# Revit family: EUBPRO-SM_Ceiling Hosted_R16_V1.0
name_source: partatom
category: Lighting Fixtures
revit_build: Autodesk Revit 2016 (Build: 20150220_1215(x64)
units: mm (PartAtom-declared; Revit-internal decimal feet)

## family parameters
Always vertical = Yes
Cut with Voids When Loaded = No
Host = Ceiling
Light Source = Yes
OmniClass Number = 23.80.70.11
OmniClass Title = Luminaries for Internal Lighting
Part Type = Normal
Room Calculation Point = No
Round Connector Dimension = Use Diameter
Shared = No
Work Plane-Based = No

## types (1)
- EUBPRO-SM-LI
    AS2293 Classification = C0=E6.3 C90=6.3
    Battery Type = Lithium Iron Phosphate 3.2V 1100mAh
    Ceiling = <By Category>
    Charging Method = Intelligent Current Limited Constant Voltage
    Color Filter = 16777215
    Construction = PC/ABS Body with PC Diffuser
    Diffuser = All directional inserts included in the box
    Dimensions = 317 x 8.7 x 157mm (Blade), 360 x 47 x 72 (Base)
    Dimming Lamp Color Temperature Shift = <None>
    Emit Shape Visible in Rendering = No
    Emit from Rectangle Length = 1219 mm
    Emit from Rectangle Width = 610 mm
    IP Rating = IP20
    Lamp = 12 x Duris E3 LED, 100,000hrs
    Mounting = Wall, Ceiling Single-Sided & Ceiling Double-Sided
    Operating Mode = Maintained
    Operating Temperature = 1 to 40C
    Operating Voltage = 240V AC; 50Hz
    Photometric Web File = ll21358 - EUBPRO-SM-LI.IES
    Power Consumption = 1.8W (Standby), 2.8W (max)
    Product Description = Economy Ultrablade Pro Blade Surface Mount Blade Exit
    Testing Mode = N/A - Manual Test Switch
    Tilt Angle = 90.00°
    Viewing Distance = 24m
    Weight = 1.0kg

## geometry (parser evidence)
native form markers: Sweep x3
no freeform markers — native parametric forms only
